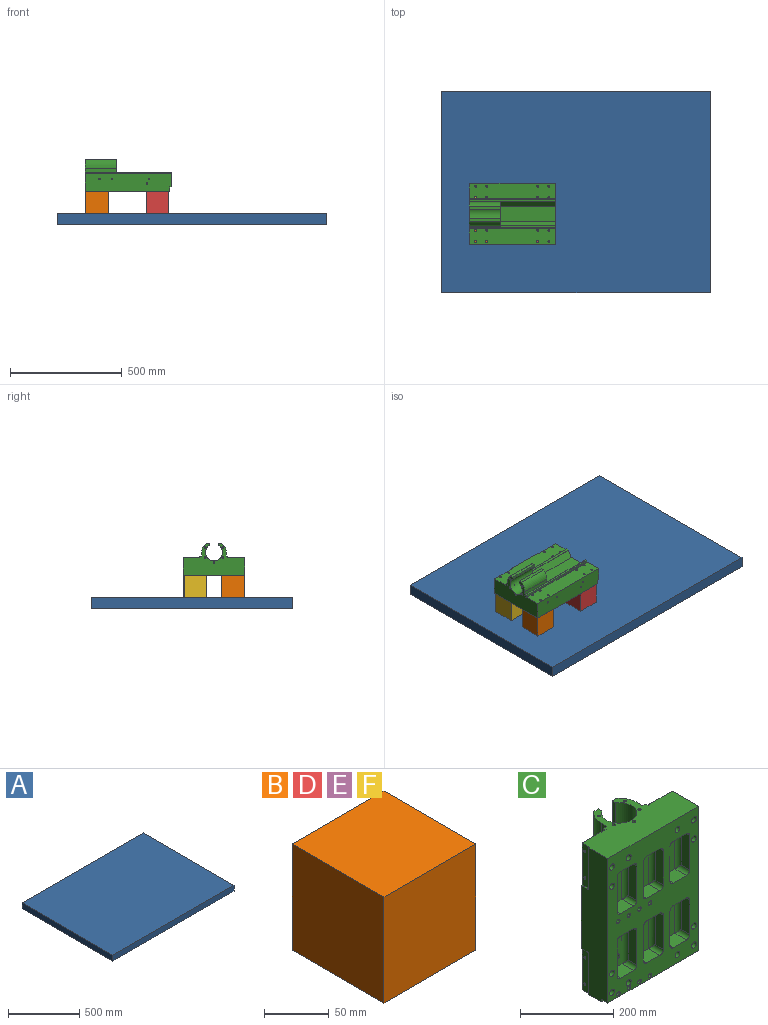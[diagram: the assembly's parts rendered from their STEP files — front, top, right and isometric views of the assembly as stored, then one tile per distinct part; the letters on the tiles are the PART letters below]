
ASSEMBLY  parts=6 mates=5
PART A: 6 faces, bbox 1200x900x50 mm
  f0: plane 1200x50mm, normal (0,1,0), area 60000mm2, adj f1,f3,f4,f5
  f1: plane 900x50mm, normal (-1,0,0), area 45000mm2, adj f0,f2,f4,f5
  f2: plane 1200x50mm, normal (0,-1,0), area 60000mm2, adj f1,f3,f4,f5
  f3: plane 900x50mm, normal (1,0,0), area 45000mm2, adj f0,f2,f4,f5
  f4: plane 1200x900mm, normal (0,0,1), area 1080000mm2, adj f0,f1,f2,f3
  f5: plane 1200x900mm, normal (0,0,-1), area 1080000mm2, adj f0,f1,f2,f3
PART B: 6 faces, bbox 100x100x100 mm
  f0: plane 100x100mm, normal (0,0,1), area 10000mm2, adj f1,f3,f4,f5
  f1: plane 100x100mm, normal (-1,0,0), area 10000mm2, adj f0,f2,f4,f5
  f2: plane 100x100mm, normal (0,0,-1), area 10000mm2, adj f1,f3,f4,f5
  f3: plane 100x100mm, normal (1,0,0), area 10000mm2, adj f0,f2,f4,f5
  f4: plane 100x100mm, normal (0,-1,0), area 10000mm2, adj f0,f1,f2,f3
  f5: plane 100x100mm, normal (0,1,0), area 10000mm2, adj f0,f1,f2,f3
PART C: 238 faces, bbox 275x144.8x385 mm
  f0: plane 139x14mm, normal (0,1,0), area 1946mm2, adj f2,f7,f10,f214
  f1: plane 378x275mm, normal (0,-1,0), area 62109.9mm2, adj f4,f6,f7,f42,f43,f44,f45,f47
  f2: plane 109.04x90mm, normal (0,0,-1), area 3910.3mm2, adj f0,f3,f8,f9,f10,f11,f12,f13
  f3: plane 139x17mm, normal (-1,0,0), area 2363mm2, adj f2,f7,f8,f24
  f4: plane 385x80mm, normal (-1,0,0), area 25610.7mm2, adj f1,f5,f7,f16,f18,f19,f198,f199
  f5: plane 275x66mm, normal (0,0,-1), area 14398.7mm2, adj f4,f6,f12,f13,f14,f15,f16,f17
  f6: plane 385x80mm, normal (1,0,0), area 30546.9mm2, adj f1,f5,f7,f17,f198,f199,f231,f233
  f7: plane 275x144.8mm, normal (0,0,1), area 23627.4mm2, adj f0,f1,f3,f4,f6,f8,f9,f10
  f8: cylinder r=54.52mm len=139mm, axis (0,0,1), area 6621mm2, adj f2,f3,f7,f9
  f9: plane 139x14mm, normal (0,1,0), area 1946mm2, adj f2,f7,f8,f213
  f10: cylinder r=54.52mm len=139mm, axis (0,0,1), area 6621mm2, adj f0,f2,f7,f11
  f11: plane 139x17mm, normal (1,0,0), area 2363mm2, adj f2,f7,f10,f22
  f12: plane 246x30mm, normal (0.85,0.52,0), area 8650mm2, adj f2,f5,f13,f23
  f13: plane 246x70mm, normal (0,1,0), area 17220mm2, adj f2,f5,f12,f14
  f14: plane 246x30mm, normal (-0.85,0.52,0), area 8650mm2, adj f2,f5,f13,f21
  f15: plane 385x8mm, normal (1,0,0), area 3080mm2, adj f5,f7,f22,f218
  f16: plane 385x69mm, normal (0,1,0), area 25396.1mm2, adj f4,f5,f7,f18,f20,f126,f129,f133
  f17: plane 385x71mm, normal (0,1,0), area 26826.1mm2, adj f5,f6,f7,f138,f141,f144,f147,f156
  f18: plane 18x3mm, normal (0,0,-1), area 54mm2, adj f4,f16,f20,f228
  f19: plane 105x3mm, normal (0,1,0), area 315mm2, adj f4,f5,f20,f228
  f20: plane 110x23mm, normal (-1,0,0), area 2467.1mm2, adj f5,f16,f18,f19,f28,f31,f228
  f21: plane 246x1.2mm, normal (-1,0,0), area 295.2mm2, adj f2,f5,f14,f22
  f22: plane 385x9.16mm, normal (0,1,0), area 3362.5mm2, adj f2,f5,f7,f11,f15,f21
  f23: plane 246x1.2mm, normal (1,0,0), area 295.2mm2, adj f2,f5,f12,f24
  f24: plane 385x11.16mm, normal (0,1,0), area 4132.5mm2, adj f2,f3,f5,f7,f23,f25
  f25: plane 385x8mm, normal (-1,0,0), area 3080mm2, adj f5,f7,f24,f215
  f26: cone r=2.5mm half-angle=59deg, axis (-1,0,0), area 22.9mm2, adj f27
  f27: cylinder r=2.5mm len=14.48mm, axis (-1,0,0), area 227.4mm2, adj f26,f28
  f28: cone r=3.02mm half-angle=45deg, axis (-1,0,0), area 12.9mm2, adj f20,f27
  f29: cone r=2.5mm half-angle=59deg, axis (-1,0,0), area 22.9mm2, adj f30
  f30: cylinder r=2.5mm len=14.48mm, axis (-1,0,0), area 227.4mm2, adj f29,f31
  f31: cone r=3.02mm half-angle=45deg, axis (-1,0,0), area 12.9mm2, adj f20,f30
  f32: cone r=3.4mm half-angle=59deg, axis (0,0,1), area 42.4mm2, adj f33
  f33: cylinder r=3.4mm len=23.8mm, axis (0,0,1), area 508.4mm2, adj f7,f32
  f34: cone r=3.4mm half-angle=59deg, axis (0,0,1), area 42.4mm2, adj f35
  f35: cylinder r=3.4mm len=23.8mm, axis (0,0,1), area 508.4mm2, adj f7,f34
  f36: cone r=3.4mm half-angle=59deg, axis (0,0,1), area 42.4mm2, adj f37
  f37: cylinder r=3.4mm len=23.8mm, axis (0,0,1), area 508.4mm2, adj f7,f36
  f38: cone r=3.4mm half-angle=59deg, axis (0,0,1), area 42.4mm2, adj f39
  f39: cylinder r=3.4mm len=23.8mm, axis (0,0,1), area 508.4mm2, adj f7,f38
  f40: cone r=3.4mm half-angle=59deg, axis (0,0,1), area 42.4mm2, adj f41
  f41: cylinder r=3.4mm len=23.8mm, axis (0,0,1), area 508.4mm2, adj f7,f40
  f42: plane 90x25mm, normal (1,0,0), area 2250mm2, adj f1,f90,f91,f92
  f43: plane 40x25mm, normal (0,0,-1), area 1000mm2, adj f1,f92,f94,f95
  f44: plane 90x25mm, normal (-1,0,0), area 2250mm2, adj f1,f95,f97,f98
  f45: plane 40x35mm, normal (0,0,1), area 1400mm2, adj f1,f46,f90,f98
  f46: plane 100x40mm, normal (0,-1,0), area 3823.3mm2, adj f45,f91,f94,f97,f155
  f47: plane 90x25mm, normal (1,0,0), area 2250mm2, adj f1,f72,f73,f74
  f48: plane 40x25mm, normal (0,0,-1), area 1000mm2, adj f1,f74,f78,f80
  f49: plane 90x25mm, normal (-1,0,0), area 2250mm2, adj f1,f75,f77,f80
  f50: plane 40x35mm, normal (0,0,1), area 1400mm2, adj f1,f51,f72,f75
  f51: plane 100x40mm, normal (0,-1,0), area 4000mm2, adj f50,f73,f77,f78
  f52: plane 90x25mm, normal (1,0,0), area 2250mm2, adj f1,f81,f82,f83
  f53: plane 40x25mm, normal (0,0,-1), area 1000mm2, adj f1,f83,f87,f89
  f54: plane 90x25mm, normal (-1,0,0), area 2250mm2, adj f1,f84,f86,f89
  f55: plane 40x35mm, normal (0,0,1), area 1400mm2, adj f1,f56,f81,f84
  f56: plane 100x40mm, normal (0,-1,0), area 3823.3mm2, adj f55,f82,f86,f87,f158
  f57: plane 40x35mm, normal (0,0,1), area 1400mm2, adj f1,f61,f99,f107
  f58: plane 90x25mm, normal (1,0,0), area 2250mm2, adj f1,f103,f106,f107
  f59: plane 40x25mm, normal (0,0,-1), area 1000mm2, adj f1,f100,f103,f104
  f60: plane 90x25mm, normal (-1,0,0), area 2250mm2, adj f1,f99,f100,f101
  f61: plane 100x40mm, normal (0,-1,0), area 3823.3mm2, adj f57,f101,f104,f106,f149
  f62: plane 90x25mm, normal (1,0,0), area 2250mm2, adj f1,f112,f115,f116
  f63: plane 40x25mm, normal (0,0,-1), area 1000mm2, adj f1,f109,f112,f113
  f64: plane 90x25mm, normal (-1,0,0), area 2250mm2, adj f1,f108,f109,f110
  f65: plane 40x35mm, normal (0,0,1), area 1400mm2, adj f1,f66,f108,f116
  f66: plane 100x40mm, normal (0,-1,0), area 4000mm2, adj f65,f110,f113,f115
  f67: plane 90x25mm, normal (1,0,0), area 2250mm2, adj f1,f121,f124,f125
  f68: plane 40x25mm, normal (0,0,-1), area 1000mm2, adj f1,f118,f121,f122
  f69: plane 90x25mm, normal (-1,0,0), area 2250mm2, adj f1,f117,f118,f119
  f70: plane 40x35mm, normal (0,0,1), area 1400mm2, adj f1,f71,f117,f125
  f71: plane 100x40mm, normal (0,-1,0), area 3823.3mm2, adj f70,f119,f122,f124,f132
  f72: cylinder r=10mm len=35mm, axis (0,1,0), area 492.7mm2, adj f1,f47,f50,f73
  f73: cylinder r=10mm len=100mm, axis (0,0,-1), area 1513.7mm2, adj f47,f51,f72,f76
  f74: cylinder r=10mm len=25mm, axis (0,1,0), area 392.7mm2, adj f1,f47,f48,f76
  f75: cylinder r=10mm len=35mm, axis (0,1,0), area 492.7mm2, adj f1,f49,f50,f77
  f76: sphere r=10mm, area 157.1mm2, adj f73,f74,f78
  f77: cylinder r=10mm len=100mm, axis (0,0,1), area 1513.7mm2, adj f49,f51,f75,f79
  f78: cylinder r=10mm len=40mm, axis (-1,0,0), area 628.3mm2, adj f48,f51,f76,f79
  f79: sphere r=10mm, area 157.1mm2, adj f77,f78,f80
  f80: cylinder r=10mm len=25mm, axis (0,1,0), area 392.7mm2, adj f1,f48,f49,f79
  f81: cylinder r=10mm len=35mm, axis (0,1,0), area 492.7mm2, adj f1,f52,f55,f82
  f82: cylinder r=10mm len=100mm, axis (0,0,-1), area 1513.7mm2, adj f52,f56,f81,f85
  f83: cylinder r=10mm len=25mm, axis (0,1,0), area 392.7mm2, adj f1,f52,f53,f85
  f84: cylinder r=10mm len=35mm, axis (0,1,0), area 492.7mm2, adj f1,f54,f55,f86
  f85: sphere r=10mm, area 157.1mm2, adj f82,f83,f87
  f86: cylinder r=10mm len=100mm, axis (0,0,1), area 1513.7mm2, adj f54,f56,f84,f88
  f87: cylinder r=10mm len=40mm, axis (-1,0,0), area 628.3mm2, adj f53,f56,f85,f88
  f88: sphere r=10mm, area 157.1mm2, adj f86,f87,f89
  f89: cylinder r=10mm len=25mm, axis (0,1,0), area 392.7mm2, adj f1,f53,f54,f88
  f90: cylinder r=10mm len=35mm, axis (0,1,0), area 492.7mm2, adj f1,f42,f45,f91
  f91: cylinder r=10mm len=100mm, axis (0,0,-1), area 1513.7mm2, adj f42,f46,f90,f93
  f92: cylinder r=10mm len=25mm, axis (0,1,0), area 392.7mm2, adj f1,f42,f43,f93
  f93: sphere r=10mm, area 157.1mm2, adj f91,f92,f94
  f94: cylinder r=10mm len=40mm, axis (-1,0,0), area 628.3mm2, adj f43,f46,f93,f96
  f95: cylinder r=10mm len=25mm, axis (0,1,0), area 392.7mm2, adj f1,f43,f44,f96
  f96: sphere r=10mm, area 157.1mm2, adj f94,f95,f97
  f97: cylinder r=10mm len=100mm, axis (0,0,1), area 1513.7mm2, adj f44,f46,f96,f98
  f98: cylinder r=10mm len=35mm, axis (0,1,0), area 492.7mm2, adj f1,f44,f45,f97
  f99: cylinder r=10mm len=35mm, axis (0,1,0), area 492.7mm2, adj f1,f57,f60,f101
  f100: cylinder r=10mm len=25mm, axis (0,1,0), area 392.7mm2, adj f1,f59,f60,f102
  f101: cylinder r=10mm len=100mm, axis (0,0,1), area 1513.7mm2, adj f60,f61,f99,f102
  f102: sphere r=10mm, area 157.1mm2, adj f100,f101,f104
  f103: cylinder r=10mm len=25mm, axis (0,1,0), area 392.7mm2, adj f1,f58,f59,f105
  f104: cylinder r=10mm len=40mm, axis (-1,0,0), area 628.3mm2, adj f59,f61,f102,f105
  f105: sphere r=10mm, area 157.1mm2, adj f103,f104,f106
  f106: cylinder r=10mm len=100mm, axis (0,0,-1), area 1513.7mm2, adj f58,f61,f105,f107
  f107: cylinder r=10mm len=35mm, axis (0,1,0), area 492.7mm2, adj f1,f57,f58,f106
  f108: cylinder r=10mm len=35mm, axis (0,1,0), area 492.7mm2, adj f1,f64,f65,f110
  f109: cylinder r=10mm len=25mm, axis (0,1,0), area 392.7mm2, adj f1,f63,f64,f111
  f110: cylinder r=10mm len=100mm, axis (0,0,-1), area 1513.7mm2, adj f64,f66,f108,f111
  f111: sphere r=10mm, area 157.1mm2, adj f109,f110,f113
  f112: cylinder r=10mm len=25mm, axis (0,1,0), area 392.7mm2, adj f1,f62,f63,f114
  f113: cylinder r=10mm len=40mm, axis (1,0,0), area 628.3mm2, adj f63,f66,f111,f114
  f114: sphere r=10mm, area 157.1mm2, adj f112,f113,f115
  f115: cylinder r=10mm len=100mm, axis (0,0,1), area 1513.7mm2, adj f62,f66,f114,f116
  f116: cylinder r=10mm len=35mm, axis (0,1,0), area 492.7mm2, adj f1,f62,f65,f115
  f117: cylinder r=10mm len=35mm, axis (0,1,0), area 492.7mm2, adj f1,f69,f70,f119
  f118: cylinder r=10mm len=25mm, axis (0,1,0), area 392.7mm2, adj f1,f68,f69,f120
  f119: cylinder r=10mm len=100mm, axis (0,0,-1), area 1513.7mm2, adj f69,f71,f117,f120
  f120: sphere r=10mm, area 157.1mm2, adj f118,f119,f122
  f121: cylinder r=10mm len=25mm, axis (0,1,0), area 392.7mm2, adj f1,f67,f68,f123
  f122: cylinder r=10mm len=40mm, axis (1,0,0), area 628.3mm2, adj f68,f71,f120,f123
  f123: sphere r=10mm, area 157.1mm2, adj f121,f122,f124
  f124: cylinder r=10mm len=100mm, axis (0,0,1), area 1513.7mm2, adj f67,f71,f123,f125
  f125: cylinder r=10mm len=35mm, axis (0,1,0), area 492.7mm2, adj f1,f67,f70,f124
  f126: cylinder r=4.5mm len=30mm, axis (0,-1,0), area 848.2mm2, adj f16,f127
  f127: plane 15x15mm, normal (0,-1,0), area 113.1mm2, adj f126,f128
  f128: cylinder r=7.5mm len=50mm, axis (0,-1,0), area 2356.2mm2, adj f1,f127
  f129: cylinder r=4.5mm len=30mm, axis (0,-1,0), area 848.2mm2, adj f16,f130
  f130: plane 15x15mm, normal (0,-1,0), area 113.1mm2, adj f129,f131
  f131: cylinder r=7.5mm len=50mm, axis (0,-1,0), area 2356.2mm2, adj f1,f130
  f132: cylinder r=7.5mm len=15mm, axis (0,-1,0), area 706.9mm2, adj f71,f134
  f133: cylinder r=4.5mm len=30mm, axis (0,-1,0), area 848.2mm2, adj f16,f134
  f134: plane 15x15mm, normal (0,-1,0), area 113.1mm2, adj f132,f133
  f135: cylinder r=4.5mm len=30mm, axis (0,-1,0), area 848.2mm2, adj f16,f136
  f136: plane 15x15mm, normal (0,-1,0), area 113.1mm2, adj f135,f137
  f137: cylinder r=7.5mm len=50mm, axis (0,-1,0), area 2356.2mm2, adj f1,f136
  f138: cylinder r=4.5mm len=30mm, axis (0,-1,0), area 848.2mm2, adj f17,f139
  f139: plane 15x15mm, normal (0,-1,0), area 113.1mm2, adj f138,f140
  f140: cylinder r=7.5mm len=50mm, axis (0,-1,0), area 2356.2mm2, adj f1,f139
  f141: cylinder r=4.5mm len=30mm, axis (0,-1,0), area 848.2mm2, adj f17,f142
  f142: plane 15x15mm, normal (0,-1,0), area 113.1mm2, adj f141,f143
  f143: cylinder r=7.5mm len=50mm, axis (0,-1,0), area 2356.2mm2, adj f1,f142
  f144: cylinder r=4.5mm len=30mm, axis (0,-1,0), area 848.2mm2, adj f17,f145
  f145: plane 15x15mm, normal (0,-1,0), area 113.1mm2, adj f144,f146
  f146: cylinder r=7.5mm len=50mm, axis (0,-1,0), area 2356.2mm2, adj f1,f145
  f147: cylinder r=4.5mm len=30mm, axis (0,-1,0), area 848.2mm2, adj f17,f148
  f148: plane 15x15mm, normal (0,-1,0), area 113.1mm2, adj f147,f149
  f149: cylinder r=7.5mm len=15mm, axis (0,-1,0), area 706.9mm2, adj f61,f148
  f150: cylinder r=4.5mm len=30mm, axis (0,-1,0), area 848.2mm2, adj f16,f151
  f151: plane 15x15mm, normal (0,-1,0), area 113.1mm2, adj f150,f152
  f152: cylinder r=7.5mm len=50mm, axis (0,-1,0), area 2356.2mm2, adj f1,f151
  f153: cylinder r=4.5mm len=30mm, axis (0,-1,0), area 848.2mm2, adj f16,f154
  f154: plane 15x15mm, normal (0,-1,0), area 113.1mm2, adj f153,f155
  f155: cylinder r=7.5mm len=15mm, axis (0,-1,0), area 706.9mm2, adj f46,f154
  f156: cylinder r=4.5mm len=30mm, axis (0,-1,0), area 848.2mm2, adj f17,f157
  f157: plane 15x15mm, normal (0,-1,0), area 113.1mm2, adj f156,f158
  f158: cylinder r=7.5mm len=15mm, axis (0,-1,0), area 706.9mm2, adj f56,f157
  f159: cylinder r=4.5mm len=30mm, axis (0,-1,0), area 848.2mm2, adj f17,f160
  f160: plane 15x15mm, normal (0,-1,0), area 113.1mm2, adj f159,f161
  f161: cylinder r=7.5mm len=50mm, axis (0,-1,0), area 2356.2mm2, adj f1,f160
  f162: cylinder r=4.5mm len=30mm, axis (0,-1,0), area 848.2mm2, adj f17,f163
  f163: plane 15x15mm, normal (0,-1,0), area 113.1mm2, adj f162,f164
  f164: cylinder r=7.5mm len=50mm, axis (0,-1,0), area 2356.2mm2, adj f1,f163
  f165: cylinder r=4.5mm len=30mm, axis (0,-1,0), area 848.2mm2, adj f17,f166
  f166: plane 15x15mm, normal (0,-1,0), area 113.1mm2, adj f165,f167
  f167: cylinder r=7.5mm len=50mm, axis (0,-1,0), area 2356.2mm2, adj f1,f166
  f168: cylinder r=4.5mm len=30mm, axis (0,-1,0), area 848.2mm2, adj f16,f169
  f169: plane 15x15mm, normal (0,-1,0), area 113.1mm2, adj f168,f170
  f170: cylinder r=7.5mm len=50mm, axis (0,-1,0), area 2356.2mm2, adj f1,f169
  f171: cylinder r=4.5mm len=30mm, axis (0,-1,0), area 848.2mm2, adj f16,f172
  f172: plane 15x15mm, normal (0,-1,0), area 113.1mm2, adj f171,f173
  f173: cylinder r=7.5mm len=50mm, axis (0,-1,0), area 2356.2mm2, adj f1,f172
  f174: cone r=4.4mm half-angle=59deg, axis (0,-1,0), area 71mm2, adj f175
  f175: cylinder r=4.4mm len=23.18mm, axis (0,-1,0), area 640.7mm2, adj f174,f176
  f176: cone r=5.03mm half-angle=45deg, axis (0,-1,0), area 26.2mm2, adj f1,f175
  f177: cone r=4.4mm half-angle=59deg, axis (0,-1,0), area 71mm2, adj f178
  f178: cylinder r=4.4mm len=23.18mm, axis (0,-1,0), area 640.7mm2, adj f177,f179
  f179: cone r=5.03mm half-angle=45deg, axis (0,-1,0), area 26.2mm2, adj f1,f178
  f180: cone r=4.4mm half-angle=59deg, axis (0,-1,0), area 71mm2, adj f181
  f181: cylinder r=4.4mm len=23.18mm, axis (0,-1,0), area 640.7mm2, adj f180,f182
  f182: cone r=5.03mm half-angle=45deg, axis (0,-1,0), area 26.2mm2, adj f1,f181
  f183: cone r=4.4mm half-angle=59deg, axis (0,-1,0), area 71mm2, adj f184
  f184: cylinder r=4.4mm len=23.18mm, axis (0,-1,0), area 640.7mm2, adj f183,f185
  f185: cone r=5.03mm half-angle=45deg, axis (0,-1,0), area 26.2mm2, adj f1,f184
  f186: cone r=4.4mm half-angle=59deg, axis (0,-1,0), area 71mm2, adj f187
  f187: cylinder r=4.4mm len=23.18mm, axis (0,-1,0), area 640.7mm2, adj f186,f188
  f188: cone r=5.03mm half-angle=45deg, axis (0,-1,0), area 26.2mm2, adj f1,f187
  f189: cone r=4.4mm half-angle=59deg, axis (0,-1,0), area 71mm2, adj f190
  f190: cylinder r=4.4mm len=23.18mm, axis (0,-1,0), area 640.7mm2, adj f189,f191
  f191: cone r=5.03mm half-angle=45deg, axis (0,-1,0), area 26.2mm2, adj f1,f190
  f192: cone r=4.4mm half-angle=59deg, axis (0,-1,0), area 71mm2, adj f193
  f193: cylinder r=4.4mm len=23.18mm, axis (0,-1,0), area 640.7mm2, adj f192,f194
  f194: cone r=5.03mm half-angle=45deg, axis (0,-1,0), area 26.2mm2, adj f1,f193
  f195: cone r=4.4mm half-angle=59deg, axis (0,-1,0), area 71mm2, adj f196
  f196: cylinder r=4.4mm len=23.18mm, axis (0,-1,0), area 640.7mm2, adj f195,f197
  f197: cone r=5.03mm half-angle=45deg, axis (0,-1,0), area 26.2mm2, adj f1,f196
  f198: plane 275x7mm, normal (0,-1,0), area 1925mm2, adj f4,f5,f6,f199
  f199: plane 275x20mm, normal (0,0,-1), area 5296.4mm2, adj f1,f4,f6,f198,f202,f205,f208,f211
  f200: cone r=3.4mm half-angle=59deg, axis (0,0,-1), area 42.4mm2, adj f201
  f201: cylinder r=3.4mm len=19.18mm, axis (0,0,-1), area 409.6mm2, adj f200,f202
  f202: cone r=4.03mm half-angle=45deg, axis (0,0,-1), area 20.6mm2, adj f199,f201
  f203: cone r=3.4mm half-angle=59deg, axis (0,0,-1), area 42.4mm2, adj f204
  f204: cylinder r=3.4mm len=19.18mm, axis (0,0,-1), area 409.6mm2, adj f203,f205
  f205: cone r=4.03mm half-angle=45deg, axis (0,0,-1), area 20.6mm2, adj f199,f204
  f206: cone r=3.4mm half-angle=59deg, axis (0,0,-1), area 42.4mm2, adj f207
  f207: cylinder r=3.4mm len=19.18mm, axis (0,0,-1), area 409.6mm2, adj f206,f208
  f208: cone r=4.03mm half-angle=45deg, axis (0,0,-1), area 20.6mm2, adj f199,f207
  f209: cone r=3.4mm half-angle=59deg, axis (0,0,-1), area 42.4mm2, adj f210
  f210: cylinder r=3.4mm len=19.18mm, axis (0,0,-1), area 409.6mm2, adj f209,f211
  f211: cone r=4.03mm half-angle=45deg, axis (0,0,-1), area 20.6mm2, adj f199,f210
  f212: cylinder r=38mm len=139mm, axis (0,0,1), area 27002.4mm2, adj f2,f7,f213,f214
  f213: plane 139x10.13mm, normal (1,0,0), area 1408mm2, adj f2,f7,f9,f212
  f214: plane 139x10.13mm, normal (-1,0,0), area 1408mm2, adj f0,f2,f7,f212
  f215: plane 385x4mm, normal (0,1,0), area 1540mm2, adj f5,f7,f25,f216
  f216: plane 385x2mm, normal (1,0,0), area 770mm2, adj f5,f7,f16,f215
  f217: plane 385x2mm, normal (-1,0,0), area 770mm2, adj f5,f7,f17,f218
  f218: plane 385x4mm, normal (0,1,0), area 1540mm2, adj f5,f7,f15,f217
  f219: plane 105x3mm, normal (0,1,0), area 315mm2, adj f4,f7,f221,f229
  f220: plane 18x3mm, normal (0,0,1), area 54mm2, adj f4,f16,f221,f229
  f221: plane 110x23mm, normal (-1,0,0), area 2467.1mm2, adj f7,f16,f219,f220,f224,f227,f229
  f222: cone r=2.5mm half-angle=59deg, axis (-1,0,0), area 22.9mm2, adj f223
  f223: cylinder r=2.5mm len=14.48mm, axis (-1,0,0), area 227.4mm2, adj f222,f224
  f224: cone r=3.02mm half-angle=45deg, axis (-1,0,0), area 12.9mm2, adj f221,f223
  f225: cone r=2.5mm half-angle=59deg, axis (-1,0,0), area 22.9mm2, adj f226
  f226: cylinder r=2.5mm len=14.48mm, axis (-1,0,0), area 227.4mm2, adj f225,f227
  f227: cone r=3.02mm half-angle=45deg, axis (-1,0,0), area 12.9mm2, adj f221,f226
  f228: cylinder r=5mm len=5mm, axis (1,0,0), area 23.6mm2, adj f4,f18,f19,f20
  f229: cylinder r=5mm len=5mm, axis (1,0,0), area 23.6mm2, adj f4,f219,f220,f221
  f230: cone r=3mm half-angle=59deg, axis (1,0,0), area 33mm2, adj f231
  f231: cylinder r=3mm len=20mm, axis (1,0,0), area 377mm2, adj f6,f230
  f232: cone r=3mm half-angle=59deg, axis (1,0,0), area 33mm2, adj f233
  f233: cylinder r=3mm len=20mm, axis (1,0,0), area 377mm2, adj f6,f232
  f234: cone r=3mm half-angle=59deg, axis (1,0,0), area 33mm2, adj f235
  f235: cylinder r=3mm len=20mm, axis (1,0,0), area 377mm2, adj f6,f234
  f236: cone r=3mm half-angle=59deg, axis (1,0,0), area 33mm2, adj f237
  f237: cylinder r=3mm len=20mm, axis (1,0,0), area 377mm2, adj f6,f236
PART D: same geometry as B
PART E: same geometry as B
PART F: same geometry as B
PLACE A t=(-385.58,40.87,903.56)mm
PLACE B rot(axis=(1,0,0),180deg) t=(-483.56,121.36,1044.37)mm
PLACE C rot(axis=(0.58,-0.58,-0.58),120deg) t=(-498.65,285.49,1085.06)mm
PLACE D rot(axis=(1,0,0),180deg) t=(-212.88,122.68,1044.37)mm
PLACE E rot(axis=(1,0,0),180deg) t=(-213.4,290.98,1044.37)mm
PLACE F rot(axis=(1,0,0),180deg) t=(-483.21,289.97,1044.37)mm
MATE planar F.f0 <-> A.f4  axis (0,0,-1) through (-445.3,339.97,953.56)mm
MATE planar D.f0 <-> A.f4  axis (0,0,-1) through (-174.97,172.68,953.56)mm
MATE planar B.f0 <-> A.f4  axis (0,0,-1) through (-445.65,171.36,953.56)mm
MATE planar E.f0 <-> A.f4  axis (0,0,-1) through (-175.48,340.98,953.56)mm
MATE planar C.f1 <-> B.f2  axis (0,0,-1) through (-445.65,196.09,1053.56)mm
